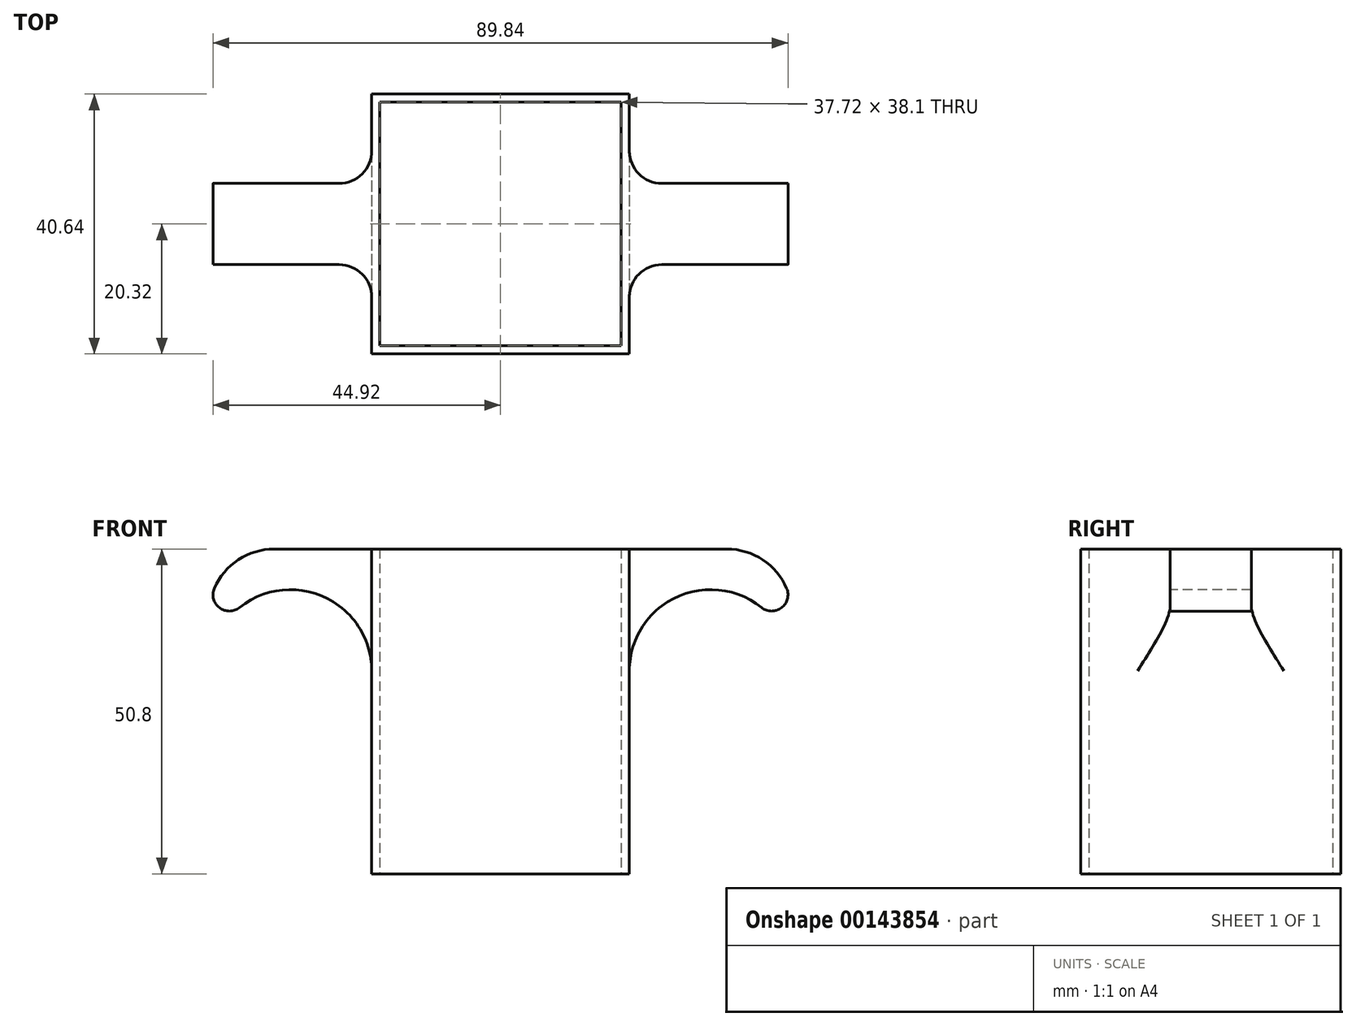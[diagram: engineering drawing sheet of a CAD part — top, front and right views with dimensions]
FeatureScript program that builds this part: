
annotation { "Feature Type Name" : "Feature", "Feature Type Description" : "" }
export const myFeature = defineFeature(function(context is Context, id is Id, definition is map)
    precondition{}
    {
        {
            var Q0;
            Q0=qCreatedBy(makeId("Top.planeOp"),FACE);
            var sketch = newSketch(context, id + "F0", { "sketchPlane" : qUnion([Q0])});
            skLineSegment(sketch, "E0.bottom", {"start": v(18.86, 19.05) * mm, "end": v(-18.86, 19.05) * mm});
            skLineSegment(sketch, "E0.top", {"start": v(18.86, -19.05) * mm, "end": v(-18.86, -19.05) * mm});
            skLineSegment(sketch, "E0.left", {"start": v(18.86, 19.05) * mm, "end": v(18.86, -19.05) * mm});
            skLineSegment(sketch, "E0.right", {"start": v(-18.86, 19.05) * mm, "end": v(-18.86, -19.05) * mm});
            skPoint(sketch, "E0.middle", {"position": v(0, 0) * mm});
            skLineSegment(sketch, "E1.bottom", {"start": v(20.13, 20.32) * mm, "end": v(-20.13, 20.32) * mm});
            skLineSegment(sketch, "E1.top", {"start": v(20.13, -20.32) * mm, "end": v(-20.13, -20.32) * mm});
            skLineSegment(sketch, "E1.left", {"start": v(20.13, 20.32) * mm, "end": v(20.13, -20.32) * mm});
            skLineSegment(sketch, "E1.right", {"start": v(-20.13, 20.32) * mm, "end": v(-20.13, -20.32) * mm});
            skSolve(sketch);
        }
        {
            var Q0;
            Q0 = qSketchRegion(id + "F0", true);
            extrude(context, id + "F1", {"entities" : qUnion([Q0]), "depth" : 50.8 * mm});
        }
        {
            var Q0;
            Q0=makeQuery(id+"F1.opExtrude","CAP_FACE",FACE,{"disambiguationData":[OSD([sQuery(id+"F0.wireOp",EDGE,"E0.bottom"),sQuery(id+"F0.wireOp",EDGE,"E0.top"),sQuery(id+"F0.wireOp",EDGE,"E0.left"),sQuery(id+"F0.wireOp",EDGE,"E0.right"),sQuery(id+"F0.wireOp",EDGE,"E1.bottom"),sQuery(id+"F0.wireOp",EDGE,"E1.top"),sQuery(id+"F0.wireOp",EDGE,"E1.left"),sQuery(id+"F0.wireOp",EDGE,"E1.right")])],"isStart":false});
            var sketch = newSketch(context, id + "F2", { "sketchPlane" : qUnion([Q0])});
            skLineSegment(sketch, "E2.bottom", {"start": v(-18.86, 6.35) * mm, "end": v(-45.53, 6.35) * mm});
            skLineSegment(sketch, "E2.top", {"start": v(-18.86, -6.35) * mm, "end": v(-45.53, -6.35) * mm});
            skLineSegment(sketch, "E2.left", {"start": v(-18.86, 6.35) * mm, "end": v(-18.86, -6.35) * mm});
            skLineSegment(sketch, "E2.right", {"start": v(-45.53, 6.35) * mm, "end": v(-45.53, -6.35) * mm});
            skPoint(sketch, "E2.middle", {"position": v(-32.2, 0) * mm});
            skLineSegment(sketch, "E3.bottom", {"start": v(45.53, 6.35) * mm, "end": v(18.86, 6.35) * mm});
            skLineSegment(sketch, "E3.top", {"start": v(45.53, -6.35) * mm, "end": v(18.86, -6.35) * mm});
            skLineSegment(sketch, "E3.left", {"start": v(45.53, 6.35) * mm, "end": v(45.53, -6.35) * mm});
            skLineSegment(sketch, "E3.right", {"start": v(18.86, 6.35) * mm, "end": v(18.86, -6.35) * mm});
            skPoint(sketch, "E3.middle", {"position": v(32.2, 0) * mm});
            skPoint(sketch, "E3.middle.positionSnap0", {"position": v(20.13, 0) * mm});
            skPoint(sketch, "E3.centerSnap0", {"position": v(20.13, 0) * mm});
            skSolve(sketch);
        }
        {
            var Q0;
            Q0 = qSketchRegion(id + "F2", true);
            extrude(context, id + "F3", {"entities" : qUnion([Q0]), "operationType" : NewBodyOperationType.ADD, "oppositeDirection" : true, "depth" : 19.05 * mm});
        }
        {
            var Q0;
            Q0=makeQuery(id+"F3.opExtrude","SWEPT_FACE",FACE,{"disambiguationData":[OSD([sQuery(id+"F2.wireOp",EDGE,"E2.top")])]});
            var sketch = newSketch(context, id + "F4", { "sketchPlane" : qUnion([Q0])});
            skArc(sketch, "E4", {"start": v(-20.13, 31.75) * mm, "mid": v(-32.83, 44.45) * mm, "end": v(-45.53, 31.75) * mm});
            skArc(sketch, "E5", {"start": v(45.53, 31.75) * mm, "mid": v(32.83, 44.45) * mm, "end": v(20.13, 31.75) * mm});
            skLineSegment(sketch, "E6", {"start": v(-45.53, 31.75) * mm, "end": v(-20.13, 31.75) * mm});
            skLineSegment(sketch, "E7", {"start": v(20.13, 31.75) * mm, "end": v(45.53, 31.75) * mm});
            skSolve(sketch);
        }
        {
            var Q0;
            Q0 = qSketchRegion(id + "F4", true);
            extrude(context, id + "F5", {"entities" : qUnion([Q0]), "operationType" : NewBodyOperationType.REMOVE, "oppositeDirection" : true, "depth" : 25.4 * mm});
        }
        {
            var Q0;
            Q0=makeQuery(id+"F3.opExtrude","CAP_EDGE",EDGE,{"disambiguationData":[OSD([sQuery(id+"F2.wireOp",EDGE,"E3.left")])],"isStart":true});
            var Q1;
            Q1=makeQuery(id+"F3.opExtrude","CAP_EDGE",EDGE,{"disambiguationData":[OSD([sQuery(id+"F2.wireOp",EDGE,"E2.right")])],"isStart":true});
            fillet(context, id + "F6", {"entities" : qUnion([Q0, Q1]), "radius" : 10.16 * mm, "tangentPropagation" : true, "allowEdgeOverflow" : false});
        }
        {
            var Q0;
            {var subQ0=sQuery(id+"F4.wireOp",EDGE,"E7");var subQ1=sQuery(id+"F4.wireOp",EDGE,"E5");Q0=makeQuery(id+"F5.boolean.opBoolean","MERGE",EDGE,{"derivedFrom":[makeQuery(id+"F3.opExtrude","CAP_EDGE",EDGE,{"disambiguationData":[OSD([sQuery(id+"F2.wireOp",EDGE,"E3.left")])],"isStart":false}),makeQuery(id+"F5.opExtrude","SWEPT_EDGE",EDGE,{"disambiguationData":[OSD([subQ1,subQ0]),TDD([makeQuery(id+"F4.imprint","INTERSECT",VERTEX,{"disambiguationData":[OD(0.0)],"derivedFrom":[subQ1,subQ0]})])]})]});}
            var Q1;
            {var subQ0=sQuery(id+"F2.wireOp",EDGE,"E2.right");Q1=makeQuery(id+"F5.boolean.opBoolean","MERGE",EDGE,{"derivedFrom":[makeQuery(id+"F3.opExtrude","CAP_EDGE",EDGE,{"disambiguationData":[OSD([subQ0])],"isStart":false}),makeQuery(id+"F5.opExtrude","SWEPT_EDGE",EDGE,{"disambiguationData":[OSD([sQuery(id+"F2.wireOp",EDGE,"E2.top"),subQ0,sQuery(id+"F4.wireOp",EDGE,"E4"),sQuery(id+"F4.wireOp",EDGE,"E6")])]})]});}
            fillet(context, id + "F7", {"entities" : qUnion([Q0, Q1]), "radius" : 2.54 * mm, "tangentPropagation" : true, "allowEdgeOverflow" : false});
        }
        {
            var Q0;
            Q0=makeQuery(id+"F3.boolean.opBoolean","INTERSECT",EDGE,{"derivedFrom":[makeQuery(id+"F1.opExtrude","SWEPT_FACE",FACE,{"disambiguationData":[OSD([sQuery(id+"F0.wireOp",EDGE,"E1.right")])]}),makeQuery(id+"F3.opExtrude","SWEPT_FACE",FACE,{"disambiguationData":[OSD([sQuery(id+"F2.wireOp",EDGE,"E2.top")])]})]});
            var Q1;
            Q1=makeQuery(id+"F3.boolean.opBoolean","INTERSECT",EDGE,{"derivedFrom":[makeQuery(id+"F1.opExtrude","SWEPT_FACE",FACE,{"disambiguationData":[OSD([sQuery(id+"F0.wireOp",EDGE,"E1.right")])]}),makeQuery(id+"F3.opExtrude","SWEPT_FACE",FACE,{"disambiguationData":[OSD([sQuery(id+"F2.wireOp",EDGE,"E2.bottom")])]})]});
            var Q2;
            Q2=makeQuery(id+"F3.boolean.opBoolean","INTERSECT",EDGE,{"derivedFrom":[makeQuery(id+"F1.opExtrude","SWEPT_FACE",FACE,{"disambiguationData":[OSD([sQuery(id+"F0.wireOp",EDGE,"E1.left")])]}),makeQuery(id+"F3.opExtrude","SWEPT_FACE",FACE,{"disambiguationData":[OSD([sQuery(id+"F2.wireOp",EDGE,"E3.bottom")])]})]});
            var Q3;
            Q3=makeQuery(id+"F3.boolean.opBoolean","INTERSECT",EDGE,{"derivedFrom":[makeQuery(id+"F1.opExtrude","SWEPT_FACE",FACE,{"disambiguationData":[OSD([sQuery(id+"F0.wireOp",EDGE,"E1.left")])]}),makeQuery(id+"F3.opExtrude","SWEPT_FACE",FACE,{"disambiguationData":[OSD([sQuery(id+"F2.wireOp",EDGE,"E3.top")])]})]});
            fillet(context, id + "F8", {"entities" : qUnion([Q0, Q1, Q2, Q3]), "radius" : 5.08 * mm, "tangentPropagation" : true, "allowEdgeOverflow" : false});
        }
    });
